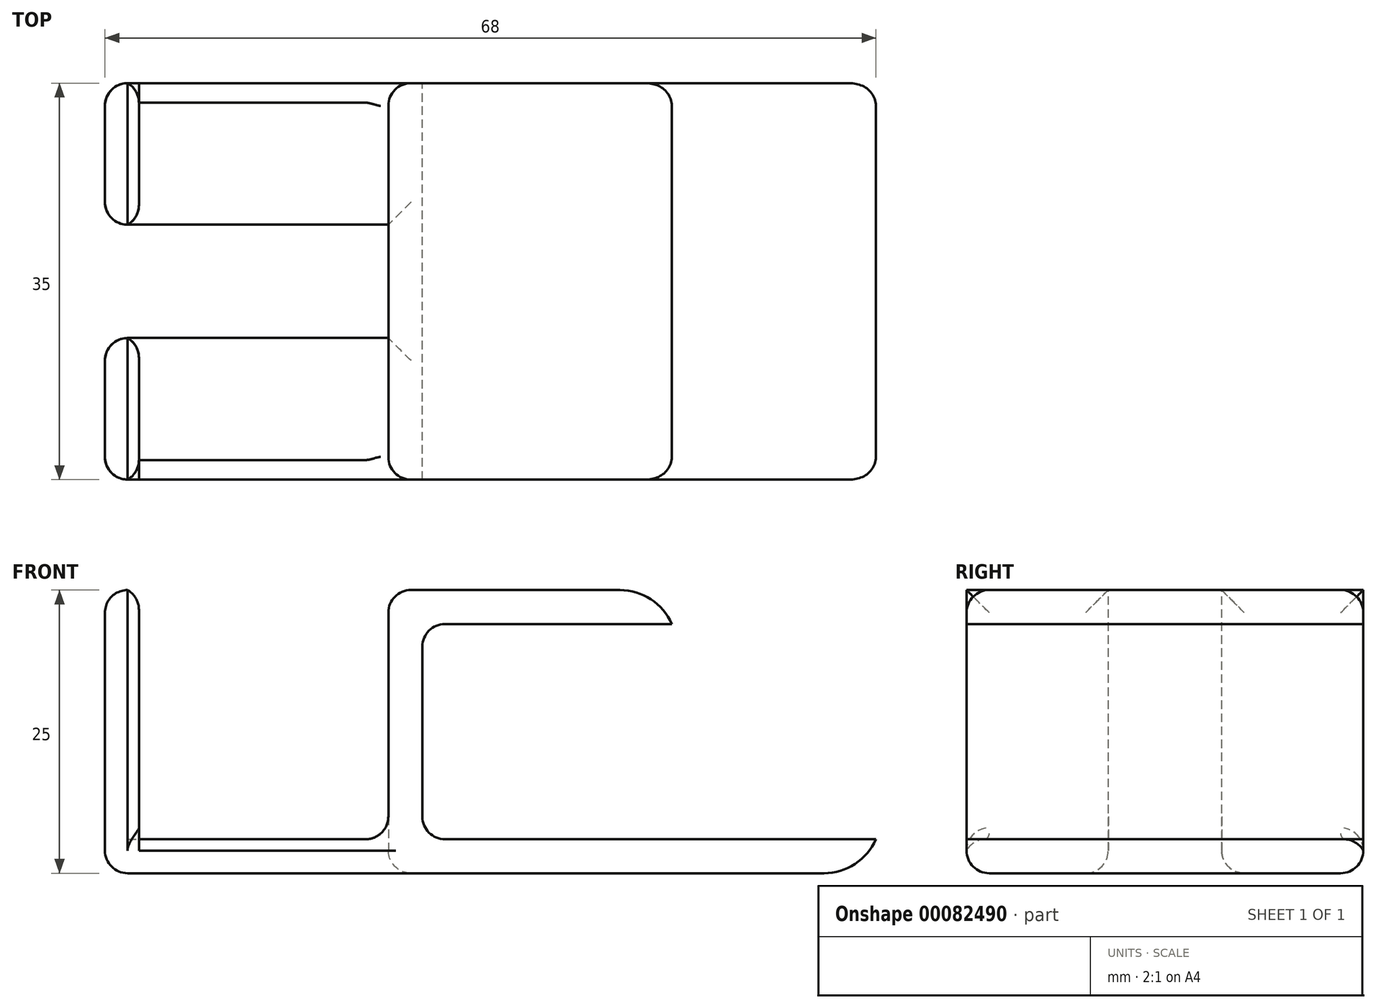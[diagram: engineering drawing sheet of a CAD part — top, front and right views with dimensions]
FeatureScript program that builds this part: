
annotation { "Feature Type Name" : "Feature", "Feature Type Description" : "" }
export const myFeature = defineFeature(function(context is Context, id is Id, definition is map)
    precondition{}
    {
        {
            assignVariable(context, id + "F0", {"name" : "totalWidth", "anyValue" : 35});
        }
        {
            var Q0;
            Q0=qCreatedBy(makeId("Front.planeOp"),FACE);
            var sketch = newSketch(context, id + "F1", { "sketchPlane" : qUnion([Q0])});
            skLineSegment(sketch, "E0.bottom", {"start": v(-34, 1.5) * mm, "end": v(34, 1.5) * mm});
            skLineSegment(sketch, "E0.top", {"start": v(-34, -1.5) * mm, "end": v(34, -1.5) * mm});
            skLineSegment(sketch, "E0.left", {"start": v(-34, 1.5) * mm, "end": v(-34, -1.5) * mm});
            skLineSegment(sketch, "E0.right", {"start": v(34, 1.5) * mm, "end": v(34, -1.5) * mm});
            skPoint(sketch, "E0.middle", {"position": v(0, 0) * mm});
            skLineSegment(sketch, "E1.bottom", {"start": v(-34, 1.5) * mm, "end": v(-31, 1.5) * mm});
            skLineSegment(sketch, "E1.top", {"start": v(-34, 23.5) * mm, "end": v(-31, 23.5) * mm});
            skLineSegment(sketch, "E1.left", {"start": v(-34, 1.5) * mm, "end": v(-34, 23.5) * mm});
            skLineSegment(sketch, "E1.right", {"start": v(-31, 1.5) * mm, "end": v(-31, 23.5) * mm});
            skLineSegment(sketch, "E2.bottom", {"start": v(-9, 1.5) * mm, "end": v(-6, 1.5) * mm});
            skLineSegment(sketch, "E2.top", {"start": v(-9, 23.5) * mm, "end": v(-6, 23.5) * mm});
            skLineSegment(sketch, "E2.left", {"start": v(-6, 1.5) * mm, "end": v(-6, 23.5) * mm});
            skLineSegment(sketch, "E2.right", {"start": v(-9, 1.5) * mm, "end": v(-9, 23.5) * mm});
            skLineSegment(sketch, "E3.bottom", {"start": v(-6, 23.5) * mm, "end": v(16, 23.5) * mm});
            skLineSegment(sketch, "E3.top", {"start": v(-6, 20.5) * mm, "end": v(16, 20.5) * mm});
            skLineSegment(sketch, "E3.left", {"start": v(-6, 23.5) * mm, "end": v(-6, 20.5) * mm});
            skLineSegment(sketch, "E3.right", {"start": v(16, 23.5) * mm, "end": v(16, 20.5) * mm});
            skSolve(sketch);
        }
        {
            var Q0;
            Q0=qSketchRegion(id+"F1",true);
            extrude(context, id + "F2", {"entities" : qUnion([Q0]), "endBound" : BoundingType.SYMMETRIC, "depth" : (getVariable(context, 'totalWidth')) * mm});
        }
        {
            var Q0;
            {var subQ0=sQuery(id+"F1.wireOp",EDGE,"E0.bottom");Q0=makeQuery(id+"F2.opExtrude","SWEPT_FACE",FACE,{"disambiguationData":[OSD([subQ0]),TDD([makeQuery(id+"F1.imprint","IMPRINT",EDGE,{"disambiguationData":[TD([[makeQuery(id+"F1.imprint","INTERSECT",VERTEX,{"derivedFrom":[subQ0,sQuery(id+"F1.wireOp",EDGE,"E1.bottom"),sQuery(id+"F1.wireOp",EDGE,"E1.right")]}),-1.0]])],"derivedFrom":subQ0})])]});}
            var sketch = newSketch(context, id + "F3", { "sketchPlane" : qUnion([Q0])});
            skLineSegment(sketch, "E4.bottom", {"start": v(-9, 5) * mm, "end": v(-45.95, 5) * mm});
            skLineSegment(sketch, "E4.top", {"start": v(-9, -5) * mm, "end": v(-45.95, -5) * mm});
            skLineSegment(sketch, "E4.left", {"start": v(-9, 5) * mm, "end": v(-9, -5) * mm});
            skLineSegment(sketch, "E4.right", {"start": v(-45.95, 5) * mm, "end": v(-45.95, -5) * mm});
            skPoint(sketch, "E5", {"position": v(-9, 0) * mm});
            skSolve(sketch);
        }
        {
            var Q0;
            {var subQ0=sQuery(id+"F3.wireOp",EDGE,"E4.right");Q0=makeQuery(id+"F3.imprint","IMPRINT",FACE,{"disambiguationData":[TD([[makeQuery(id+"F3.imprint","IMPRINT",EDGE,{"derivedFrom":subQ0}),1.0]])]});}
            var Q1;
            {var subQ0=sQuery(id+"F3.wireOp",EDGE,"E4.left");Q1=makeQuery(id+"F3.imprint","IMPRINT",FACE,{"disambiguationData":[TD([[makeQuery(id+"F3.imprint","IMPRINT",EDGE,{"derivedFrom":subQ0}),1.0]])]});}
            extrude(context, id + "F4", {"entities" : qUnion([Q0, Q1]), "operationType" : NewBodyOperationType.REMOVE, "endBound" : BoundingType.SYMMETRIC, "depth" : 130.8 * mm});
        }
        {
            var Q0;
            Q0=makeQuery(id+"F2.opExtrude","SWEPT_EDGE",EDGE,{"disambiguationData":[OSD([sQuery(id+"F1.wireOp",EDGE,"E3.bottom"),sQuery(id+"F1.wireOp",EDGE,"E3.right")])]});
            var Q1;
            Q1=makeQuery(id+"F2.opExtrude","SWEPT_EDGE",EDGE,{"disambiguationData":[OSD([sQuery(id+"F1.wireOp",EDGE,"E0.top"),sQuery(id+"F1.wireOp",EDGE,"E0.right")])]});
            fillet(context, id + "F5", {"entities" : qUnion([Q0, Q1]), "radius" : 5 * mm, "tangentPropagation" : true, "allowEdgeOverflow" : false});
        }
        {
            var Q0;
            {var subQ0=sQuery(id+"F1.wireOp",EDGE,"E2.right");var subQ2=sQuery(id+"F1.wireOp",EDGE,"E0.bottom");var subQ3=sQuery(id+"F1.wireOp",EDGE,"E2.bottom");Q0=makeQuery(id+"F4.boolean.opBoolean","SPLIT",EDGE,{"disambiguationData":[TD([makeQuery(id+"F4.opExtrude","SWEPT_FACE",FACE,{"disambiguationData":[OSD([sQuery(id+"F3.wireOp",EDGE,"E4.top")])]})])],"derivedFrom":makeQuery(id+"F2.opExtrude","SWEPT_EDGE",EDGE,{"disambiguationData":[OSD([subQ2,subQ3,subQ0])]})});}
            var Q1;
            {var subQ0=sQuery(id+"F1.wireOp",EDGE,"E2.right");var subQ2=sQuery(id+"F1.wireOp",EDGE,"E0.bottom");var subQ3=sQuery(id+"F1.wireOp",EDGE,"E2.bottom");Q1=makeQuery(id+"F4.boolean.opBoolean","SPLIT",EDGE,{"disambiguationData":[TD([makeQuery(id+"F4.opExtrude","SWEPT_FACE",FACE,{"disambiguationData":[OSD([sQuery(id+"F3.wireOp",EDGE,"E4.bottom")])]})])],"derivedFrom":makeQuery(id+"F2.opExtrude","SWEPT_EDGE",EDGE,{"disambiguationData":[OSD([subQ2,subQ3,subQ0])]})});}
            fillet(context, id + "F6", {"entities" : qUnion([Q0, Q1]), "radius" : 2 * mm, "allowEdgeOverflow" : false});
        }
        {
            var Q0;
            Q0=makeQuery(id+"F2.opExtrude","SWEPT_EDGE",EDGE,{"disambiguationData":[OSD([sQuery(id+"F1.wireOp",EDGE,"E2.top"),sQuery(id+"F1.wireOp",EDGE,"E2.right")])]});
            fillet(context, id + "F7", {"entities" : qUnion([Q0]), "radius" : 2 * mm, "tangentPropagation" : true, "allowEdgeOverflow" : false});
        }
        {
            var Q0;
            Q0=makeQuery(id+"F2.opExtrude","CAP_EDGE",EDGE,{"disambiguationData":[OSD([sQuery(id+"F1.wireOp",EDGE,"E2.top"),sQuery(id+"F1.wireOp",EDGE,"E3.bottom")])],"isStart":false});
            var Q1;
            Q1=makeQuery(id+"F2.opExtrude","CAP_EDGE",EDGE,{"disambiguationData":[OSD([sQuery(id+"F1.wireOp",EDGE,"E2.top"),sQuery(id+"F1.wireOp",EDGE,"E3.bottom")])],"isStart":true});
            var Q2;
            Q2=makeQuery(id+"F2.opExtrude","CAP_EDGE",EDGE,{"disambiguationData":[OSD([sQuery(id+"F1.wireOp",EDGE,"E0.top")])],"isStart":true});
            var Q3;
            Q3=makeQuery(id+"F2.opExtrude","CAP_EDGE",EDGE,{"disambiguationData":[OSD([sQuery(id+"F1.wireOp",EDGE,"E0.top")])],"isStart":false});
            var Q4;
            {var subQ1=sQuery(id+"F1.wireOp",EDGE,"E0.left");var subQ2=sQuery(id+"F1.wireOp",EDGE,"E0.top");Q4=makeQuery(id+"F4.boolean.opBoolean","SPLIT",EDGE,{"disambiguationData":[TD([makeQuery(id+"F4.opExtrude","SWEPT_FACE",FACE,{"disambiguationData":[OSD([sQuery(id+"F3.wireOp",EDGE,"E4.bottom")])]})])],"derivedFrom":makeQuery(id+"F2.opExtrude","SWEPT_EDGE",EDGE,{"disambiguationData":[OSD([subQ2,subQ1])]})});}
            var Q5;
            {var subQ1=sQuery(id+"F1.wireOp",EDGE,"E0.left");var subQ2=sQuery(id+"F1.wireOp",EDGE,"E0.top");Q5=makeQuery(id+"F4.boolean.opBoolean","SPLIT",EDGE,{"disambiguationData":[TD([makeQuery(id+"F4.opExtrude","SWEPT_FACE",FACE,{"disambiguationData":[OSD([sQuery(id+"F3.wireOp",EDGE,"E4.top")])]})])],"derivedFrom":makeQuery(id+"F2.opExtrude","SWEPT_EDGE",EDGE,{"disambiguationData":[OSD([subQ2,subQ1])]})});}
            var Q6;
            Q6=makeQuery(id+"F4.boolean.opBoolean","INTERSECT",EDGE,{"derivedFrom":[makeQuery(id+"F2.opExtrude","SWEPT_FACE",FACE,{"disambiguationData":[OSD([sQuery(id+"F1.wireOp",EDGE,"E0.top")])]}),makeQuery(id+"F4.opExtrude","SWEPT_FACE",FACE,{"disambiguationData":[OSD([sQuery(id+"F3.wireOp",EDGE,"E4.top")])]})]});
            var Q7;
            Q7=makeQuery(id+"F4.boolean.opBoolean","INTERSECT",EDGE,{"derivedFrom":[makeQuery(id+"F2.opExtrude","SWEPT_FACE",FACE,{"disambiguationData":[OSD([sQuery(id+"F1.wireOp",EDGE,"E0.top")])]}),makeQuery(id+"F4.opExtrude","SWEPT_FACE",FACE,{"disambiguationData":[OSD([sQuery(id+"F3.wireOp",EDGE,"E4.bottom")])]})]});
            var Q8;
            Q8=makeQuery(id+"F4.boolean.opBoolean","INTERSECT",EDGE,{"derivedFrom":[makeQuery(id+"F2.opExtrude","SWEPT_FACE",FACE,{"disambiguationData":[OSD([sQuery(id+"F1.wireOp",EDGE,"E0.top")])]}),makeQuery(id+"F4.opExtrude","SWEPT_FACE",FACE,{"disambiguationData":[OSD([sQuery(id+"F3.wireOp",EDGE,"E4.left")])]})]});
            fillet(context, id + "F8", {"entities" : qUnion([Q0, Q1, Q2, Q3, Q4, Q5, Q6, Q7, Q8]), "radius" : 2 * mm, "tangentPropagation" : true, "allowEdgeOverflow" : false});
        }
        {
            var Q0;
            {var subQ0=sQuery(id+"F1.wireOp",EDGE,"E1.left");var subQ1=sQuery(id+"F1.wireOp",EDGE,"E1.top");Q0=makeQuery(id+"F4.boolean.opBoolean","SPLIT",EDGE,{"disambiguationData":[TD([makeQuery(id+"F4.opExtrude","SWEPT_FACE",FACE,{"disambiguationData":[OSD([sQuery(id+"F3.wireOp",EDGE,"E4.bottom")])]})])],"derivedFrom":makeQuery(id+"F2.opExtrude","SWEPT_EDGE",EDGE,{"disambiguationData":[OSD([subQ1,subQ0])]})});}
            var Q1;
            {var subQ0=sQuery(id+"F1.wireOp",EDGE,"E1.left");var subQ1=sQuery(id+"F1.wireOp",EDGE,"E1.top");Q1=makeQuery(id+"F4.boolean.opBoolean","SPLIT",EDGE,{"disambiguationData":[TD([makeQuery(id+"F4.opExtrude","SWEPT_FACE",FACE,{"disambiguationData":[OSD([sQuery(id+"F3.wireOp",EDGE,"E4.top")])]})])],"derivedFrom":makeQuery(id+"F2.opExtrude","SWEPT_EDGE",EDGE,{"disambiguationData":[OSD([subQ1,subQ0])]})});}
            var Q2;
            Q2=makeQuery(id+"F4.boolean.opBoolean","INTERSECT",EDGE,{"derivedFrom":[makeQuery(id+"F2.opExtrude","SWEPT_FACE",FACE,{"disambiguationData":[OSD([sQuery(id+"F1.wireOp",EDGE,"E0.left"),sQuery(id+"F1.wireOp",EDGE,"E1.left")])]}),makeQuery(id+"F4.opExtrude","SWEPT_FACE",FACE,{"disambiguationData":[OSD([sQuery(id+"F3.wireOp",EDGE,"E4.top")])]})]});
            var Q3;
            Q3=makeQuery(id+"F2.opExtrude","CAP_EDGE",EDGE,{"disambiguationData":[OSD([sQuery(id+"F1.wireOp",EDGE,"E0.left"),sQuery(id+"F1.wireOp",EDGE,"E1.left")])],"isStart":false});
            var Q4;
            Q4=makeQuery(id+"F2.opExtrude","CAP_EDGE",EDGE,{"disambiguationData":[OSD([sQuery(id+"F1.wireOp",EDGE,"E0.left"),sQuery(id+"F1.wireOp",EDGE,"E1.left")])],"isStart":true});
            var Q5;
            Q5=makeQuery(id+"F4.boolean.opBoolean","INTERSECT",EDGE,{"derivedFrom":[makeQuery(id+"F2.opExtrude","SWEPT_FACE",FACE,{"disambiguationData":[OSD([sQuery(id+"F1.wireOp",EDGE,"E0.left"),sQuery(id+"F1.wireOp",EDGE,"E1.left")])]}),makeQuery(id+"F4.opExtrude","SWEPT_FACE",FACE,{"disambiguationData":[OSD([sQuery(id+"F3.wireOp",EDGE,"E4.bottom")])]})]});
            fillet(context, id + "F9", {"entities" : qUnion([Q0, Q1, Q2, Q3, Q4, Q5]), "radius" : 2 * mm, "tangentPropagation" : true, "allowEdgeOverflow" : false});
        }
        {
            var Q0;
            {var subQ0=sQuery(id+"F1.wireOp",EDGE,"E1.right");var subQ1=sQuery(id+"F1.wireOp",EDGE,"E1.top");Q0=makeQuery(id+"F4.boolean.opBoolean","SPLIT",EDGE,{"disambiguationData":[TD([makeQuery(id+"F4.opExtrude","SWEPT_FACE",FACE,{"disambiguationData":[OSD([sQuery(id+"F3.wireOp",EDGE,"E4.bottom")])]})])],"derivedFrom":makeQuery(id+"F2.opExtrude","SWEPT_EDGE",EDGE,{"disambiguationData":[OSD([subQ1,subQ0])]})});}
            var Q1;
            {var subQ0=sQuery(id+"F1.wireOp",EDGE,"E1.right");var subQ1=sQuery(id+"F1.wireOp",EDGE,"E1.top");Q1=makeQuery(id+"F4.boolean.opBoolean","SPLIT",EDGE,{"disambiguationData":[TD([makeQuery(id+"F4.opExtrude","SWEPT_FACE",FACE,{"disambiguationData":[OSD([sQuery(id+"F3.wireOp",EDGE,"E4.top")])]})])],"derivedFrom":makeQuery(id+"F2.opExtrude","SWEPT_EDGE",EDGE,{"disambiguationData":[OSD([subQ1,subQ0])]})});}
            var Q2;
            Q2=makeQuery(id+"F4.boolean.opBoolean","INTERSECT",EDGE,{"derivedFrom":[makeQuery(id+"F2.opExtrude","SWEPT_FACE",FACE,{"disambiguationData":[OSD([sQuery(id+"F1.wireOp",EDGE,"E1.right")])]}),makeQuery(id+"F4.opExtrude","SWEPT_FACE",FACE,{"disambiguationData":[OSD([sQuery(id+"F3.wireOp",EDGE,"E4.bottom")])]})]});
            var Q3;
            Q3=makeQuery(id+"F2.opExtrude","CAP_EDGE",EDGE,{"disambiguationData":[OSD([sQuery(id+"F1.wireOp",EDGE,"E1.right")])],"isStart":false});
            var Q4;
            Q4=makeQuery(id+"F4.boolean.opBoolean","INTERSECT",EDGE,{"derivedFrom":[makeQuery(id+"F2.opExtrude","SWEPT_FACE",FACE,{"disambiguationData":[OSD([sQuery(id+"F1.wireOp",EDGE,"E1.right")])]}),makeQuery(id+"F4.opExtrude","SWEPT_FACE",FACE,{"disambiguationData":[OSD([sQuery(id+"F3.wireOp",EDGE,"E4.top")])]})]});
            var Q5;
            Q5=makeQuery(id+"F2.opExtrude","CAP_EDGE",EDGE,{"disambiguationData":[OSD([sQuery(id+"F1.wireOp",EDGE,"E1.right")])],"isStart":true});
            fillet(context, id + "F10", {"entities" : qUnion([Q0, Q1, Q2, Q3, Q4, Q5]), "radius" : 2 * mm, "tangentPropagation" : true, "allowEdgeOverflow" : false});
        }
        {
            var Q0;
            Q0=makeQuery(id+"F2.opExtrude","SWEPT_EDGE",EDGE,{"disambiguationData":[OSD([sQuery(id+"F1.wireOp",EDGE,"E0.bottom"),sQuery(id+"F1.wireOp",EDGE,"E2.bottom"),sQuery(id+"F1.wireOp",EDGE,"E2.left")])]});
            var Q1;
            Q1=makeQuery(id+"F2.opExtrude","SWEPT_EDGE",EDGE,{"disambiguationData":[OSD([sQuery(id+"F1.wireOp",EDGE,"E2.left"),sQuery(id+"F1.wireOp",EDGE,"E3.top"),sQuery(id+"F1.wireOp",EDGE,"E3.left")])]});
            fillet(context, id + "F11", {"entities" : qUnion([Q0, Q1]), "radius" : 2 * mm, "tangentPropagation" : true, "allowEdgeOverflow" : false});
        }
    });
